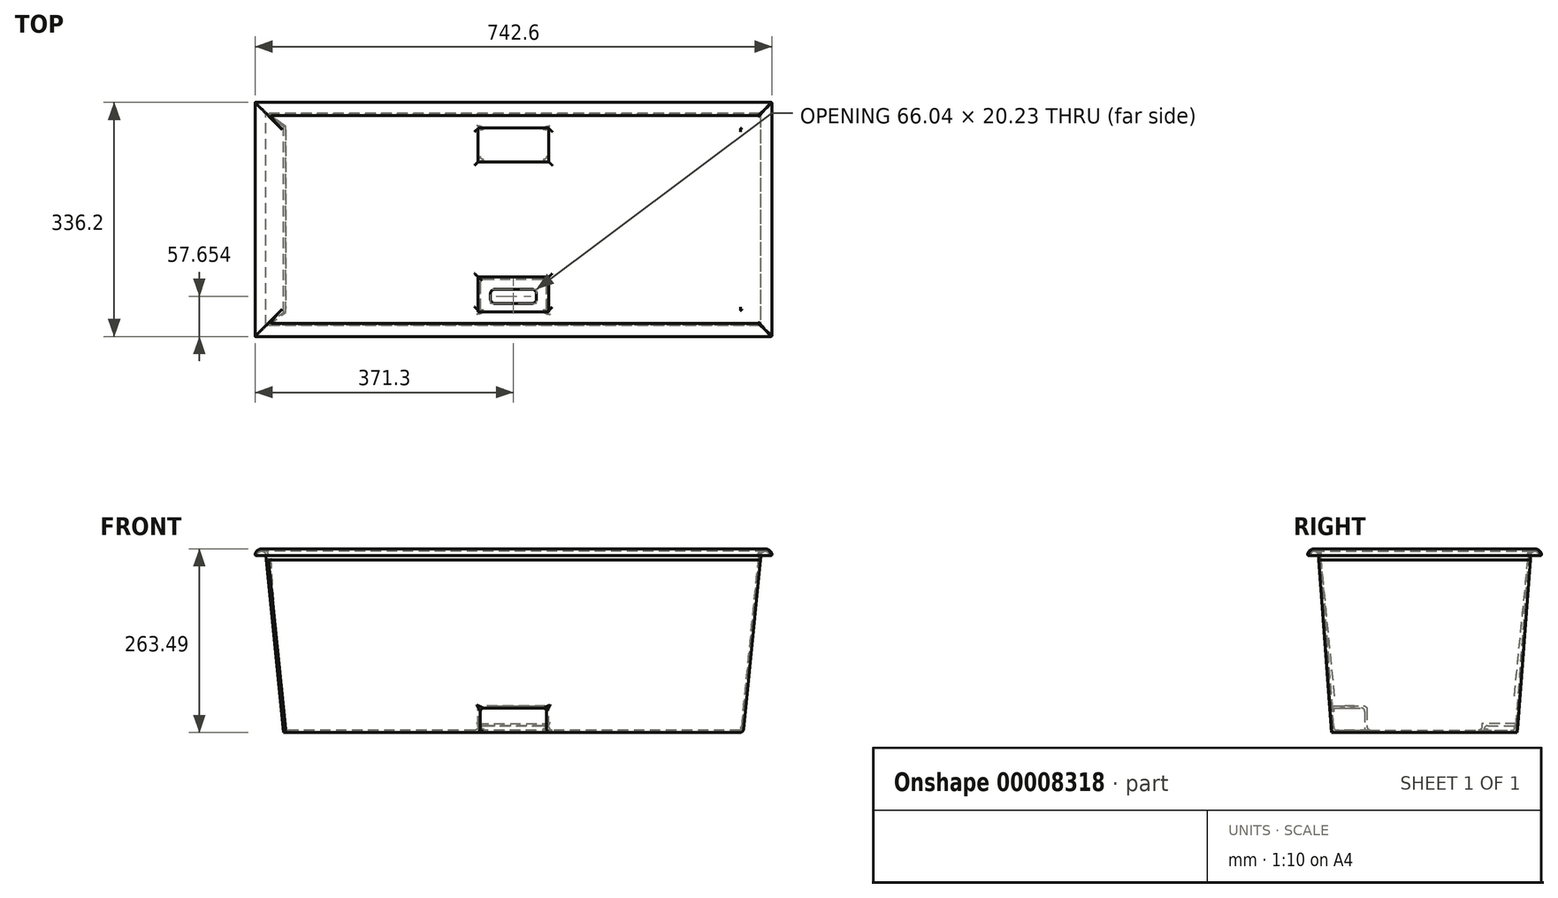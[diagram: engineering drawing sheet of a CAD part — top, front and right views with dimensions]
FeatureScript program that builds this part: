
annotation { "Feature Type Name" : "Feature", "Feature Type Description" : "" }
export const myFeature = defineFeature(function(context is Context, id is Id, definition is map)
    precondition{}
    {
        {
            var Q0;
            Q0=qCreatedBy(makeId("Top.planeOp"),FACE);
            var sketch = newSketch(context, id + "F0", { "sketchPlane" : qUnion([Q0])});
            skLineSegment(sketch, "E0", {"start": v(0, 0) * mm, "end": v(-542.8, 0) * mm, "construction": true});
            skLineSegment(sketch, "E1", {"start": v(0, 0) * mm, "end": v(0, 202.17) * mm, "construction": true});
            skLineSegment(sketch, "E2.bottom", {"start": v(-355.6, 152.4) * mm, "end": v(355.6, 152.4) * mm});
            skLineSegment(sketch, "E2.top", {"start": v(-355.6, -152.4) * mm, "end": v(355.6, -152.4) * mm});
            skLineSegment(sketch, "E2.left", {"start": v(-355.6, 152.4) * mm, "end": v(-355.6, -152.4) * mm});
            skLineSegment(sketch, "E2.right", {"start": v(355.6, 152.4) * mm, "end": v(355.6, -152.4) * mm});
            skLineSegment(sketch, "E3.0", {"start": v(-368.3, 165.1) * mm, "end": v(-368.3, -165.1) * mm});
            skLineSegment(sketch, "E3.1", {"start": v(-368.3, 165.1) * mm, "end": v(368.3, 165.1) * mm});
            skLineSegment(sketch, "E3.2", {"start": v(368.3, 165.1) * mm, "end": v(368.3, -165.1) * mm});
            skLineSegment(sketch, "E3.3", {"start": v(-368.3, -165.1) * mm, "end": v(368.3, -165.1) * mm});
            skSolve(sketch);
        }
        {
            var Q0;
            Q0=qCreatedBy(makeId("Right.planeOp"),FACE);
            var sketch = newSketch(context, id + "F1", { "sketchPlane" : qUnion([Q0])});
            skPoint(sketch, "E4.0", {"position": v(-165.1, 0) * mm});
            skLineSegment(sketch, "E4.1", {"start": v(165.1, 0) * mm, "end": v(161.94, 0) * mm});
            skPoint(sketch, "E4.2", {"position": v(-152.4, 0) * mm});
            skPoint(sketch, "E4.3", {"position": v(0, 0) * mm});
            skPoint(sketch, "E4.4", {"position": v(165.1, 0) * mm});
            skLineSegment(sketch, "E5", {"start": v(-152.4, 0) * mm, "end": v(-133.35, -254) * mm});
            skLineSegment(sketch, "E6", {"start": v(-133.35, -254) * mm, "end": v(133.35, -254) * mm});
            skLineSegment(sketch, "E7", {"start": v(133.35, -254) * mm, "end": v(152.4, 0) * mm});
            skLineSegment(sketch, "E8.0", {"start": v(130.4, -250.83) * mm, "end": v(149.26, 0.6) * mm});
            skLineSegment(sketch, "E8.1", {"start": v(-130.4, -250.83) * mm, "end": v(130.4, -250.82) * mm});
            skLineSegment(sketch, "E8.2", {"start": v(-149.23, 0.24) * mm, "end": v(-130.4, -250.83) * mm});
            skArc(sketch, "E9", {"start": v(165.1, 0) * mm, "mid": v(157.17, 7.93) * mm, "end": v(149.24, 0) * mm});
            skLineSegment(sketch, "E10.trimOffspring", {"start": v(149.24, 0) * mm, "end": v(0, 0) * mm});
            skArc(sketch, "E11", {"start": v(161.94, 0) * mm, "mid": v(157.17, 4.77) * mm, "end": v(152.4, 0) * mm});
            skLineSegment(sketch, "E12", {"start": v(152.4, 0) * mm, "end": v(152.4, 0) * mm});
            skArc(sketch, "E13.0.MirrorCS", {"start": v(-165.1, 0) * mm, "mid": v(-157.17, 7.93) * mm, "end": v(-149.24, 0) * mm});
            skArc(sketch, "E14.0.MirrorCS", {"start": v(-161.94, 0) * mm, "mid": v(-157.17, 4.77) * mm, "end": v(-152.4, 0) * mm});
            skLineSegment(sketch, "E15.0.MirrorCS", {"start": v(-165.1, 0) * mm, "end": v(-161.94, 0) * mm});
            skLineSegment(sketch, "E16.trimOffspring", {"start": v(-161.94, 0) * mm, "end": v(-165.1, 0) * mm});
            skLineSegment(sketch, "E17.trimOffspring", {"start": v(-149.22, 0) * mm, "end": v(-152.4, 0) * mm});
            skLineSegment(sketch, "E18", {"start": v(-152.4, 0) * mm, "end": v(152.4, 0) * mm});
            skSolve(sketch);
        }
        {
            var Q0;
            Q0=qCreatedBy(makeId("Front.planeOp"),FACE);
            var sketch = newSketch(context, id + "F2", { "sketchPlane" : qUnion([Q0])});
            skPoint(sketch, "E19.0", {"position": v(0, -254) * mm});
            skPoint(sketch, "E19.1", {"position": v(-355.6, 0) * mm});
            skPoint(sketch, "E19.2", {"position": v(355.6, 0) * mm});
            skPoint(sketch, "E19.4", {"position": v(-368.3, 0) * mm});
            skLineSegment(sketch, "E19.5", {"start": v(-368.3, 0) * mm, "end": v(-365.15, 0) * mm});
            skLineSegment(sketch, "E20", {"start": v(-330.2, -254) * mm, "end": v(330.2, -254) * mm});
            skLineSegment(sketch, "E21", {"start": v(-355.6, 0) * mm, "end": v(-330.2, -254) * mm});
            skLineSegment(sketch, "E22", {"start": v(330.2, -254) * mm, "end": v(355.6, 0) * mm});
            skArc(sketch, "E23", {"start": v(-352.49, 0.79) * mm, "mid": v(-360.77, 7.92) * mm, "end": v(-368.3, 0) * mm});
            skLineSegment(sketch, "E24.0", {"start": v(327.33, -250.83) * mm, "end": v(352.5, 0.94) * mm});
            skLineSegment(sketch, "E24.1", {"start": v(-327.33, -250.83) * mm, "end": v(327.33, -250.83) * mm});
            skLineSegment(sketch, "E24.2", {"start": v(-352.49, 0.79) * mm, "end": v(-327.33, -250.83) * mm});
            skArc(sketch, "E25", {"start": v(-355.6, 0) * mm, "mid": v(-360.37, 4.77) * mm, "end": v(-365.15, 0) * mm});
            skArc(sketch, "E26", {"start": v(368.3, 0) * mm, "mid": v(361.95, 6.35) * mm, "end": v(355.6, 0) * mm});
            skArc(sketch, "E27", {"start": v(371.44, 0) * mm, "mid": v(362.42, 9.48) * mm, "end": v(352.5, 0.94) * mm});
            skLineSegment(sketch, "E28", {"start": v(368.3, 0) * mm, "end": v(371.44, 0) * mm});
            skPoint(sketch, "E29.end.orphan", {"position": v(0, -250.83) * mm});
            skLineSegment(sketch, "E30", {"start": v(355.6, 0) * mm, "end": v(-355.6, 0) * mm});
            skSolve(sketch);
        }
        {
            var Q0;
            {var subQ6=sQuery(id+"F1.wireOp",EDGE,"E5");Q0=makeQuery(id+"F1.imprint","IMPRINT",FACE,{"disambiguationData":[TD([[makeQuery(id+"F1.imprint","IMPRINT",EDGE,{"derivedFrom":subQ6}),1.0]])]});}
            var Q1;
            {var subQ5=sQuery(id+"F1.wireOp",EDGE,"E8.1");Q1=makeQuery(id+"F1.imprint","IMPRINT",FACE,{"disambiguationData":[TD([[makeQuery(id+"F1.imprint","IMPRINT",EDGE,{"derivedFrom":subQ5}),1.0]])]});}
            extrude(context, id + "F3", {"entities" : qUnion([Q0, Q1]), "endBound" : BoundingType.SYMMETRIC, "depth" : 762 * mm});
        }
        {
            var Q0;
            Q0=makeQuery(id+"F2.imprint","IMPRINT",FACE,{"disambiguationData":[TD([[makeQuery(id+"F2.imprint","IMPRINT",EDGE,{"derivedFrom":sQuery(id+"F2.wireOp",EDGE,"E20")}),1.0]])]});
            var Q1;
            {var subQ5=sQuery(id+"F2.wireOp",EDGE,"E24.1");Q1=makeQuery(id+"F2.imprint","IMPRINT",FACE,{"disambiguationData":[TD([[makeQuery(id+"F2.imprint","IMPRINT",EDGE,{"derivedFrom":subQ5}),1.0]])]});}
            extrude(context, id + "F4", {"entities" : qUnion([Q0, Q1]), "endBound" : BoundingType.SYMMETRIC, "depth" : 406.4 * mm});
        }
        {
            var Q0;
            Q0=makeQuery(id+"F3.opExtrude","SWEPT_BODY",BODY,{"disambiguationData":[OSD([sQuery(id+"F1.wireOp",EDGE,"E5"),sQuery(id+"F1.wireOp",EDGE,"E6"),sQuery(id+"F1.wireOp",EDGE,"E7"),sQuery(id+"F1.wireOp",EDGE,"E18")])]});
            var Q1;
            Q1=makeQuery(id+"F4.opExtrude","SWEPT_BODY",BODY,{"disambiguationData":[OSD([sQuery(id+"F2.wireOp",EDGE,"E20"),sQuery(id+"F2.wireOp",EDGE,"E21"),sQuery(id+"F2.wireOp",EDGE,"E22"),sQuery(id+"F2.wireOp",EDGE,"E30")])]});
            booleanBodies(context, id + "F5", {"operationType" : BooleanOperationType.INTERSECTION, "tools" : qUnion([Q0, Q1])});
        }
        {
            var Q0;
            Q0=makeQuery(id+"F3.opExtrude","SWEPT_FACE",FACE,{"disambiguationData":[OSD([sQuery(id+"F1.wireOp",EDGE,"E18")])]});
            shell(context, id + "F6", {"entities" : qUnion([Q0]), "thickness" : 3.17 * mm});
        }
        {
            var Q0;
            {var subQ3=sQuery(id+"F2.wireOp",EDGE,"E26");Q0=makeQuery(id+"F2.imprint","IMPRINT",FACE,{"disambiguationData":[TD([[makeQuery(id+"F2.imprint","IMPRINT",EDGE,{"derivedFrom":subQ3}),-1.0]])]});}
            var Q1;
            Q1=sQuery(id+"F0.wireOp",EDGE,"E2.right");
            var Q2;
            Q2=sQuery(id+"F0.wireOp",EDGE,"E2.top");
            var Q3;
            Q3=sQuery(id+"F0.wireOp",EDGE,"E2.left");
            var Q4;
            Q4=sQuery(id+"F0.wireOp",EDGE,"E2.bottom");
            sweep(context, id + "F7", {"operationType" : NewBodyOperationType.ADD, "profiles" : qUnion([Q0]), "path" : qUnion([Q1, Q2, Q3, Q4])});
        }
        {
            var Q0;
            Q0=makeQuery(id+"F3.opExtrude","SWEPT_FACE",FACE,{"disambiguationData":[OSD([sQuery(id+"F1.wireOp",EDGE,"E6")])]});
            var sketch = newSketch(context, id + "F8", { "sketchPlane" : qUnion([Q0])});
            skLineSegment(sketch, "E31.bottom", {"start": v(-50.8, 133.35) * mm, "end": v(50.8, 133.35) * mm});
            skLineSegment(sketch, "E31.top", {"start": v(-50.8, 82.55) * mm, "end": v(50.8, 82.55) * mm});
            skLineSegment(sketch, "E31.left", {"start": v(-50.8, 133.35) * mm, "end": v(-50.8, 82.55) * mm});
            skLineSegment(sketch, "E31.right", {"start": v(50.8, 133.35) * mm, "end": v(50.8, 82.55) * mm});
            skLineSegment(sketch, "E32.bottom", {"start": v(-50.8, -133.35) * mm, "end": v(50.8, -133.35) * mm});
            skLineSegment(sketch, "E32.top", {"start": v(-50.8, -82.55) * mm, "end": v(50.8, -82.55) * mm});
            skLineSegment(sketch, "E32.left", {"start": v(-50.8, -133.35) * mm, "end": v(-50.8, -82.55) * mm});
            skLineSegment(sketch, "E32.right", {"start": v(50.8, -133.35) * mm, "end": v(50.8, -82.55) * mm});
            skSolve(sketch);
        }
        {
            var Q0;
            Q0=makeQuery(id+"F8.imprint","IMPRINT",FACE,{"disambiguationData":[TD([[makeQuery(id+"F8.imprint","IMPRINT",EDGE,{"derivedFrom":sQuery(id+"F8.wireOp",EDGE,"E31.bottom")}),1.0]])]});
            extrude(context, id + "F9", {"entities" : qUnion([Q0]), "operationType" : NewBodyOperationType.ADD, "oppositeDirection" : true, "depth" : 38.1 * mm + 1 / 203.2 * mm});
        }
        {
            var Q0;
            Q0=makeQuery(id+"F8.imprint","IMPRINT",FACE,{"disambiguationData":[TD([[makeQuery(id+"F8.imprint","IMPRINT",EDGE,{"derivedFrom":sQuery(id+"F8.wireOp",EDGE,"E32.bottom")}),-1.0]])]});
            extrude(context, id + "F10", {"entities" : qUnion([Q0]), "operationType" : NewBodyOperationType.ADD, "oppositeDirection" : true, "depth" : 12.7 * mm});
        }
        {
            var Q0;
            Q0=makeQuery(id+"F3.opExtrude","SWEPT_FACE",FACE,{"disambiguationData":[OSD([sQuery(id+"F1.wireOp",EDGE,"E6")])]});
            var Q1;
            Q1=makeQuery(id+"F3.opExtrude","SWEPT_FACE",FACE,{"disambiguationData":[OSD([sQuery(id+"F1.wireOp",EDGE,"E5")])]});
            var Q2;
            Q2=makeQuery(id+"F4.opExtrude","SWEPT_FACE",FACE,{"disambiguationData":[OSD([sQuery(id+"F2.wireOp",EDGE,"E22")])]});
            var Q3;
            Q3=makeQuery(id+"F3.opExtrude","SWEPT_FACE",FACE,{"disambiguationData":[OSD([sQuery(id+"F1.wireOp",EDGE,"E7")])]});
            shell(context, id + "F11", {"entities" : qUnion([Q0, Q1, Q2, Q3]), "thickness" : 3.17 * mm});
        }
        {
            var Q0;
            Q0=makeQuery(id+"F4.opExtrude","SWEPT_EDGE",EDGE,{"disambiguationData":[OSD([sQuery(id+"F2.wireOp",EDGE,"E20"),sQuery(id+"F2.wireOp",EDGE,"E21")])]});
            var Q1;
            {var subQ0=sQuery(id+"F1.wireOp",EDGE,"E6");var subQ1=sQuery(id+"F1.wireOp",EDGE,"E7");Q1=makeQuery(id+"F11.opShell","OFFSET_EDGE",EDGE,{"disambiguationData":[OSD([subQ0,subQ1]),TDD([makeQuery(id+"F10.boolean.opBoolean","SPLIT",EDGE,{"disambiguationData":[TD([makeQuery(id+"F6.opShell","OFFSET_FACE",FACE,{"disambiguationData":[OSD([sQuery(id+"F2.wireOp",EDGE,"E21")])]})])],"derivedFrom":makeQuery(id+"F6.opShell","OFFSET_EDGE",EDGE,{"disambiguationData":[OSD([subQ0,subQ1])]})})])]});}
            var Q2;
            Q2=makeQuery(id+"F11.opShell","OFFSET_EDGE",EDGE,{"disambiguationData":[OSD([sQuery(id+"F1.wireOp",EDGE,"E6"),sQuery(id+"F8.wireOp",EDGE,"E32.left")])]});
            var Q3;
            Q3=makeQuery(id+"F11.opShell","OFFSET_EDGE",EDGE,{"disambiguationData":[OSD([sQuery(id+"F1.wireOp",EDGE,"E6"),sQuery(id+"F8.wireOp",EDGE,"E32.top")])]});
            var Q4;
            Q4=makeQuery(id+"F11.opShell","OFFSET_EDGE",EDGE,{"disambiguationData":[OSD([sQuery(id+"F1.wireOp",EDGE,"E6"),sQuery(id+"F8.wireOp",EDGE,"E32.right")])]});
            var Q5;
            {var subQ0=sQuery(id+"F1.wireOp",EDGE,"E6");var subQ1=sQuery(id+"F1.wireOp",EDGE,"E7");Q5=makeQuery(id+"F11.opShell","OFFSET_EDGE",EDGE,{"disambiguationData":[OSD([subQ0,subQ1]),TDD([makeQuery(id+"F10.boolean.opBoolean","SPLIT",EDGE,{"disambiguationData":[TD([makeQuery(id+"F6.opShell","OFFSET_FACE",FACE,{"disambiguationData":[OSD([sQuery(id+"F2.wireOp",EDGE,"E22")])]})])],"derivedFrom":makeQuery(id+"F6.opShell","OFFSET_EDGE",EDGE,{"disambiguationData":[OSD([subQ0,subQ1])]})})])]});}
            var Q6;
            Q6=makeQuery(id+"F11.opShell","OFFSET_EDGE",EDGE,{"disambiguationData":[OSD([sQuery(id+"F1.wireOp",EDGE,"E7"),sQuery(id+"F8.wireOp",EDGE,"E32.bottom"),sQuery(id+"F8.wireOp",EDGE,"E32.top"),sQuery(id+"F8.wireOp",EDGE,"E32.left"),sQuery(id+"F8.wireOp",EDGE,"E32.right")])]});
            var Q7;
            Q7=makeQuery(id+"F11.opShell","OFFSET_EDGE",EDGE,{"disambiguationData":[OSD([sQuery(id+"F2.wireOp",EDGE,"E20"),sQuery(id+"F2.wireOp",EDGE,"E22")])]});
            var Q8;
            {var subQ0=sQuery(id+"F1.wireOp",EDGE,"E5");var subQ1=sQuery(id+"F1.wireOp",EDGE,"E6");Q8=makeQuery(id+"F11.opShell","OFFSET_EDGE",EDGE,{"disambiguationData":[OSD([subQ0,subQ1]),TDD([makeQuery(id+"F9.boolean.opBoolean","SPLIT",EDGE,{"disambiguationData":[TD([makeQuery(id+"F6.opShell","OFFSET_FACE",FACE,{"disambiguationData":[OSD([sQuery(id+"F2.wireOp",EDGE,"E22")])]})])],"derivedFrom":makeQuery(id+"F6.opShell","OFFSET_EDGE",EDGE,{"disambiguationData":[OSD([subQ0,subQ1])]})})])]});}
            var Q9;
            Q9=makeQuery(id+"F11.opShell","OFFSET_EDGE",EDGE,{"disambiguationData":[OSD([sQuery(id+"F1.wireOp",EDGE,"E5"),sQuery(id+"F8.wireOp",EDGE,"E31.bottom"),sQuery(id+"F8.wireOp",EDGE,"E31.top"),sQuery(id+"F8.wireOp",EDGE,"E31.left"),sQuery(id+"F8.wireOp",EDGE,"E31.right")])]});
            var Q10;
            Q10=makeQuery(id+"F11.opShell","OFFSET_EDGE",EDGE,{"disambiguationData":[OSD([sQuery(id+"F1.wireOp",EDGE,"E5"),sQuery(id+"F8.wireOp",EDGE,"E31.right")])]});
            var Q11;
            Q11=makeQuery(id+"F11.opShell","OFFSET_EDGE",EDGE,{"disambiguationData":[OSD([sQuery(id+"F1.wireOp",EDGE,"E5"),sQuery(id+"F8.wireOp",EDGE,"E31.left")])]});
            var Q12;
            {var subQ0=sQuery(id+"F1.wireOp",EDGE,"E5");var subQ1=sQuery(id+"F1.wireOp",EDGE,"E6");Q12=makeQuery(id+"F11.opShell","OFFSET_EDGE",EDGE,{"disambiguationData":[OSD([subQ0,subQ1]),TDD([makeQuery(id+"F9.boolean.opBoolean","SPLIT",EDGE,{"disambiguationData":[TD([makeQuery(id+"F6.opShell","OFFSET_FACE",FACE,{"disambiguationData":[OSD([sQuery(id+"F2.wireOp",EDGE,"E21")])]})])],"derivedFrom":makeQuery(id+"F6.opShell","OFFSET_EDGE",EDGE,{"disambiguationData":[OSD([subQ0,subQ1])]})})])]});}
            fillet(context, id + "F12", {"entities" : qUnion([Q0, Q1, Q2, Q3, Q4, Q5, Q6, Q7, Q8, Q9, Q10, Q11, Q12]), "radius" : 5.08 * mm, "tangentPropagation" : true, "allowEdgeOverflow" : false});
        }
        {
            var Q0;
            Q0=makeQuery(id+"F11.opShell","OFFSET_EDGE",EDGE,{"disambiguationData":[OSD([sQuery(id+"F1.wireOp",EDGE,"E5"),sQuery(id+"F2.wireOp",EDGE,"E22")])]});
            var Q1;
            Q1=makeQuery(id+"F11.opShell","OFFSET_EDGE",EDGE,{"disambiguationData":[OSD([sQuery(id+"F1.wireOp",EDGE,"E7"),sQuery(id+"F2.wireOp",EDGE,"E22")])]});
            var Q2;
            Q2=makeQuery(id+"F11.opShell","OFFSET_EDGE",EDGE,{"disambiguationData":[OSD([sQuery(id+"F1.wireOp",EDGE,"E7"),sQuery(id+"F8.wireOp",EDGE,"E32.right")])]});
            var Q3;
            Q3=makeQuery(id+"F11.opShell","OFFSET_EDGE",EDGE,{"disambiguationData":[OSD([sQuery(id+"F8.wireOp",EDGE,"E32.top"),sQuery(id+"F8.wireOp",EDGE,"E32.right")])]});
            var Q4;
            Q4=makeQuery(id+"F11.opShell","OFFSET_EDGE",EDGE,{"disambiguationData":[OSD([sQuery(id+"F8.wireOp",EDGE,"E32.top"),sQuery(id+"F8.wireOp",EDGE,"E32.left")])]});
            var Q5;
            Q5=makeQuery(id+"F11.opShell","OFFSET_EDGE",EDGE,{"disambiguationData":[OSD([sQuery(id+"F1.wireOp",EDGE,"E7"),sQuery(id+"F8.wireOp",EDGE,"E32.left")])]});
            var Q6;
            Q6=makeQuery(id+"F11.opShell","OFFSET_EDGE",EDGE,{"disambiguationData":[OSD([sQuery(id+"F1.wireOp",EDGE,"E6"),sQuery(id+"F8.wireOp",EDGE,"E31.left")])]});
            var Q7;
            Q7=makeQuery(id+"F11.opShell","OFFSET_EDGE",EDGE,{"disambiguationData":[OSD([sQuery(id+"F1.wireOp",EDGE,"E6"),sQuery(id+"F8.wireOp",EDGE,"E31.top")])]});
            var Q8;
            Q8=makeQuery(id+"F11.opShell","OFFSET_EDGE",EDGE,{"disambiguationData":[OSD([sQuery(id+"F1.wireOp",EDGE,"E6"),sQuery(id+"F8.wireOp",EDGE,"E31.right")])]});
            var Q9;
            Q9=makeQuery(id+"F11.opShell","OFFSET_EDGE",EDGE,{"disambiguationData":[OSD([sQuery(id+"F8.wireOp",EDGE,"E31.top")])]});
            var Q10;
            Q10=makeQuery(id+"F11.opShell","OFFSET_EDGE",EDGE,{"disambiguationData":[OSD([sQuery(id+"F8.wireOp",EDGE,"E31.top"),sQuery(id+"F8.wireOp",EDGE,"E31.left")])]});
            var Q11;
            Q11=makeQuery(id+"F11.opShell","OFFSET_EDGE",EDGE,{"disambiguationData":[OSD([sQuery(id+"F8.wireOp",EDGE,"E31.left")])]});
            var Q12;
            Q12=makeQuery(id+"F11.opShell","OFFSET_EDGE",EDGE,{"disambiguationData":[OSD([sQuery(id+"F8.wireOp",EDGE,"E31.right")])]});
            var Q13;
            Q13=makeQuery(id+"F11.opShell","OFFSET_EDGE",EDGE,{"disambiguationData":[OSD([sQuery(id+"F8.wireOp",EDGE,"E31.top"),sQuery(id+"F8.wireOp",EDGE,"E31.right")])]});
            var Q14;
            Q14=makeQuery(id+"F11.opShell","OFFSET_EDGE",EDGE,{"disambiguationData":[OSD([sQuery(id+"F8.wireOp",EDGE,"E32.top")])]});
            fillet(context, id + "F13", {"entities" : qUnion([Q0, Q1, Q2, Q3, Q4, Q5, Q6, Q7, Q8, Q9, Q10, Q11, Q12, Q13, Q14]), "radius" : 5.08 * mm, "tangentPropagation" : true, "allowEdgeOverflow" : false});
        }
        {
            var Q0;
            {var subQ0=sQuery(id+"F1.wireOp",EDGE,"E7");var subQ1=sQuery(id+"F8.wireOp",EDGE,"E32.right");Q0=makeQuery(id+"F13.opFillet","BLEND_EDGE",EDGE,{"blendedFrom":[makeQuery(id+"F11.opShell","OFFSET_EDGE",EDGE,{"disambiguationData":[OSD([subQ0,subQ1])]}),makeQuery(id+"F12.opFillet","BLEND_FACE",FACE,{"disambiguationData":[OSD([subQ0,sQuery(id+"F8.wireOp",EDGE,"E32.bottom"),sQuery(id+"F8.wireOp",EDGE,"E32.top"),sQuery(id+"F8.wireOp",EDGE,"E32.left"),subQ1])]})],"blendedInto":[makeQuery(id+"F12.opFillet","BLEND_FACE",FACE,{"disambiguationData":[OSD([subQ0,sQuery(id+"F8.wireOp",EDGE,"E32.bottom"),sQuery(id+"F8.wireOp",EDGE,"E32.top"),sQuery(id+"F8.wireOp",EDGE,"E32.left"),subQ1])]})]});}
            var Q1;
            {var subQ0=sQuery(id+"F1.wireOp",EDGE,"E7");var subQ1=sQuery(id+"F8.wireOp",EDGE,"E32.left");Q1=makeQuery(id+"F13.opFillet","BLEND_EDGE",EDGE,{"blendedFrom":[makeQuery(id+"F11.opShell","OFFSET_EDGE",EDGE,{"disambiguationData":[OSD([subQ0,subQ1])]}),makeQuery(id+"F12.opFillet","BLEND_FACE",FACE,{"disambiguationData":[OSD([subQ0,sQuery(id+"F8.wireOp",EDGE,"E32.bottom"),sQuery(id+"F8.wireOp",EDGE,"E32.top"),subQ1,sQuery(id+"F8.wireOp",EDGE,"E32.right")])]})],"blendedInto":[makeQuery(id+"F12.opFillet","BLEND_FACE",FACE,{"disambiguationData":[OSD([subQ0,sQuery(id+"F8.wireOp",EDGE,"E32.bottom"),sQuery(id+"F8.wireOp",EDGE,"E32.top"),subQ1,sQuery(id+"F8.wireOp",EDGE,"E32.right")])]})]});}
            fillet(context, id + "F14", {"entities" : qUnion([Q0, Q1]), "radius" : 5.08 * mm, "tangentPropagation" : true, "allowEdgeOverflow" : false});
        }
        {
            var Q0;
            Q0=makeQuery(id+"F7.opSweep","SWEPT_FACE",FACE,{"disambiguationData":[OSD([sQuery(id+"F0.wireOp",EDGE,"E2.right"),sQuery(id+"F2.wireOp",EDGE,"E28")])]});
            fillet(context, id + "F15", {"entities" : qUnion([Q0]), "radius" : 1.5 * mm, "tangentPropagation" : true, "allowEdgeOverflow" : false});
        }
        {
            var Q0;
            Q0=makeQuery(id+"F6.opShell","OFFSET_FACE",FACE,{"disambiguationData":[OSD([sQuery(id+"F1.wireOp",EDGE,"E6")])]});
            var Q1;
            Q1=makeQuery(id+"F6.opShell","OFFSET_EDGE",EDGE,{"disambiguationData":[OSD([sQuery(id+"F1.wireOp",EDGE,"E5"),sQuery(id+"F2.wireOp",EDGE,"E22")])]});
            var Q2;
            Q2=makeQuery(id+"F6.opShell","OFFSET_EDGE",EDGE,{"disambiguationData":[OSD([sQuery(id+"F1.wireOp",EDGE,"E7"),sQuery(id+"F2.wireOp",EDGE,"E22")])]});
            var Q3;
            Q3=makeQuery(id+"F6.opShell","OFFSET_EDGE",EDGE,{"disambiguationData":[OSD([sQuery(id+"F1.wireOp",EDGE,"E5"),sQuery(id+"F2.wireOp",EDGE,"E21")])]});
            var Q4;
            Q4=makeQuery(id+"F6.opShell","OFFSET_EDGE",EDGE,{"disambiguationData":[OSD([sQuery(id+"F1.wireOp",EDGE,"E7"),sQuery(id+"F2.wireOp",EDGE,"E21")])]});
            var Q5;
            Q5=makeQuery(id+"F9.opExtrude","CAP_EDGE",EDGE,{"disambiguationData":[OSD([sQuery(id+"F8.wireOp",EDGE,"E31.right")])],"isStart":false});
            var Q6;
            Q6=makeQuery(id+"F9.opExtrude","CAP_EDGE",EDGE,{"disambiguationData":[OSD([sQuery(id+"F8.wireOp",EDGE,"E31.top")])],"isStart":false});
            var Q7;
            Q7=makeQuery(id+"F9.opExtrude","CAP_EDGE",EDGE,{"disambiguationData":[OSD([sQuery(id+"F8.wireOp",EDGE,"E31.left")])],"isStart":false});
            fillet(context, id + "F16", {"entities" : qUnion([Q0, Q1, Q2, Q3, Q4, Q5, Q6, Q7]), "radius" : 5.08 * mm, "tangentPropagation" : true, "allowEdgeOverflow" : false});
        }
        {
            var Q0;
            Q0=makeQuery(id+"F9.opExtrude","CAP_FACE",FACE,{"disambiguationData":[OSD([sQuery(id+"F8.wireOp",EDGE,"E31.bottom"),sQuery(id+"F8.wireOp",EDGE,"E31.top"),sQuery(id+"F8.wireOp",EDGE,"E31.left"),sQuery(id+"F8.wireOp",EDGE,"E31.right")])],"isStart":false});
            var sketch = newSketch(context, id + "F17", { "sketchPlane" : qUnion([Q0])});
            skLineSegment(sketch, "E33.bottom", {"start": v(-45.72, -87.63) * mm, "end": v(45.72, -87.63) * mm, "construction": true});
            skLineSegment(sketch, "E33.top", {"start": v(-45.72, -133.26) * mm, "end": v(45.72, -133.26) * mm, "construction": true});
            skLineSegment(sketch, "E33.left", {"start": v(-45.72, -87.63) * mm, "end": v(-45.72, -133.26) * mm, "construction": true});
            skLineSegment(sketch, "E33.right", {"start": v(45.72, -87.63) * mm, "end": v(45.72, -133.26) * mm, "construction": true});
            skLineSegment(sketch, "E34.0", {"start": v(33.02, -106.68) * mm, "end": v(33.02, -114.21) * mm});
            skLineSegment(sketch, "E34.1", {"start": v(-26.67, -100.33) * mm, "end": v(26.67, -100.33) * mm});
            skLineSegment(sketch, "E34.2", {"start": v(-33.02, -106.68) * mm, "end": v(-33.02, -114.21) * mm});
            skLineSegment(sketch, "E34.3", {"start": v(-26.67, -120.56) * mm, "end": v(26.67, -120.56) * mm});
            skPoint(sketch, "E35.visualSharp", {"position": v(33.02, -120.56) * mm});
            skArc(sketch, "E35.filletArc", {"start": v(26.67, -120.56) * mm, "mid": v(31.16, -118.7) * mm, "end": v(33.02, -114.21) * mm});
            skPoint(sketch, "E36.visualSharp", {"position": v(33.02, -100.33) * mm});
            skArc(sketch, "E36.filletArc", {"start": v(33.02, -106.68) * mm, "mid": v(31.16, -102.19) * mm, "end": v(26.67, -100.33) * mm});
            skPoint(sketch, "E37.visualSharp", {"position": v(-33.02, -120.56) * mm});
            skArc(sketch, "E37.filletArc", {"start": v(-33.02, -114.21) * mm, "mid": v(-31.16, -118.7) * mm, "end": v(-26.67, -120.56) * mm});
            skPoint(sketch, "E38.visualSharp", {"position": v(-33.02, -100.33) * mm});
            skArc(sketch, "E38.filletArc", {"start": v(-26.67, -100.33) * mm, "mid": v(-31.16, -102.19) * mm, "end": v(-33.02, -106.68) * mm});
            skSolve(sketch);
        }
        {
            var Q0;
            Q0=makeQuery(id+"F17.imprint","IMPRINT",FACE,{"disambiguationData":[TD([[makeQuery(id+"F17.imprint","IMPRINT",EDGE,{"derivedFrom":sQuery(id+"F17.wireOp",EDGE,"E34.0")}),-1.0]])]});
            extrude(context, id + "F18", {"entities" : qUnion([Q0]), "operationType" : NewBodyOperationType.REMOVE, "endBound" : BoundingType.THROUGH_ALL, "oppositeDirection" : true, "depth" : 25.4 * mm});
        }
    });
